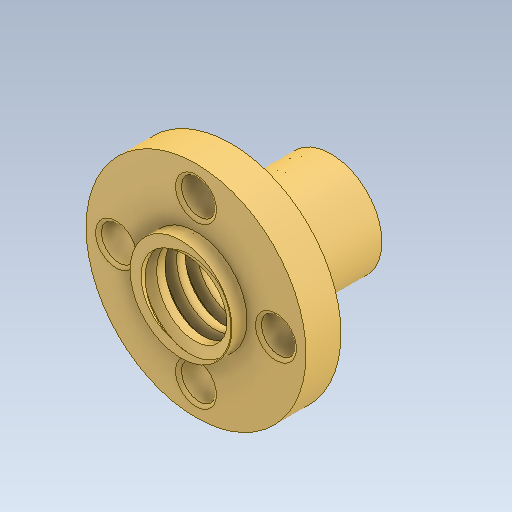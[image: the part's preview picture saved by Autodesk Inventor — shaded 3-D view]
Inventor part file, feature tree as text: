
AUTODESK INVENTOR PART (.ipt)
format: ipt  version: 2020 (Build 240168000, 168)  size: 288,768 bytes
history: mixed  units: in
note: dims shown in document units (in); Inventor stores cm internally (conversion verified against a paired STEP export)
features: fillet x1, imported_body x1
ambient origin geometry x8: Origin, YZ Plane, XZ Plane, XY Plane, X Axis, Y Axis, Z Axis, Center Point
bodies: Solid1 (imported_parasolid)
feature tree (2):
  fillet  "Fillet2"  [1 undecoded]
  imported_body  NMx_Import_Brep_tag  [imported B-rep: ~6 faces, bbox_mm=None]
note: 1 required parameter value undecoded (feature->parameter linkage not recoverable at this tier; creation-order binding heuristic only, values carry confidence <= 0.55)
